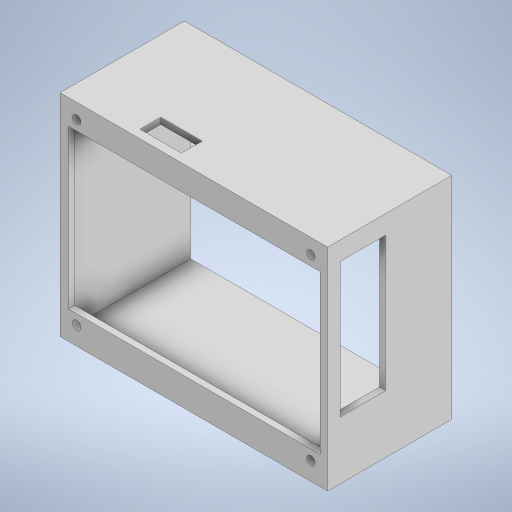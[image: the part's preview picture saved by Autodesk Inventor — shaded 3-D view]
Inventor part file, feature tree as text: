
AUTODESK INVENTOR PART (.ipt)
format: ipt  version: 2023 (Build 270158000, 158)  size: 642,560 bytes
history: native  units: mm
features: extrude x8, sketch x8
ambient origin geometry x8: Origin, YZ Plane, XZ Plane, XY Plane, X Axis, Y Axis, Z Axis, Center Point
bodies: Solid1 (feature_tree)
feature tree (16):
  extrude  "Extrusion1"  Depth=60.0mm
  extrude  "Extrusion2"  Depth=76.4mm
  extrude  "Extrusion4"  Depth=2.0mm
  extrude  "Extrusion6"  Depth=4.0mm
  extrude  "Extrusion7"  Depth=4.0mm
  extrude  "Extrusion8"  Depth=4.0mm
  extrude  "Extrusion9"  Depth=6.02mm
  extrude  "Extrusion10"  Depth=3.0mm
  sketch  "Sketch1"  dims[d0=125.15mm d1=60.0mm]
  sketch  "Sketch2"  dims[d2=100.0mm d3=0.0mm d4=76.4mm]
  sketch  "Sketch5"  dims[d5=121.51mm d7=2.0mm]
  sketch  "Sketch7"  dims[d15=10.0mm d16=4.0mm]
  sketch  "Sketch8"  dims[d17=4.765mm d18=4.0mm]
  sketch  "Sketch9"  dims[d19=85.93mm d21=4.0mm]
  sketch  "Sketch10"  dims[d22=113.11mm d23=6.02mm]
  sketch  "Sketch11"  dims[d24=4.0mm d25=4.765mm d26=113.11mm d27=3.0mm d28=0.0mm d35=7.0mm d37=6.0mm d38=22.0mm d39=65.0mm d40=10.0mm d41=0.0mm d46=1.0mm d47=4.0mm d48=1.0mm d49=1.0mm d50=57.0mm d51=0.0mm d52=2.0mm d53=0.0mm d54=2.0mm d55=0.0mm d56=2.0mm d57=0.0mm d58=64.575mm d59=10.0mm d60=20.0mm d61=4.0mm d62=10.0mm d63=3.0mm d64=0.0mm d33=0.5mm d34=0.872665mm d36=0.872665mm]
